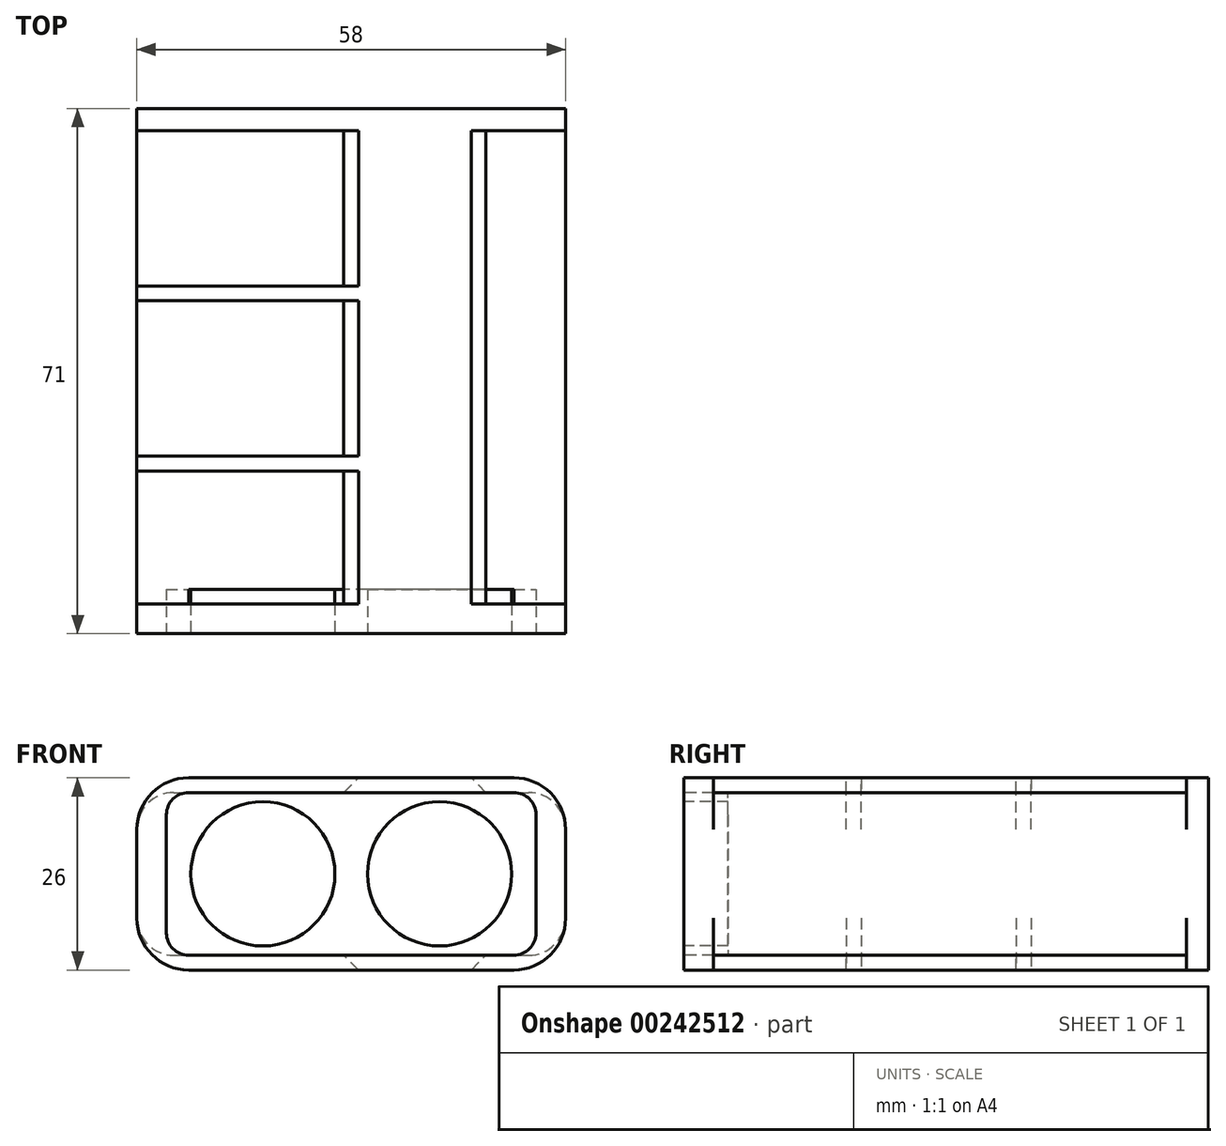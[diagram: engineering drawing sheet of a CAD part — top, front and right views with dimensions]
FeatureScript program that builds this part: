
annotation { "Feature Type Name" : "Feature", "Feature Type Description" : "" }
export const myFeature = defineFeature(function(context is Context, id is Id, definition is map)
    precondition{}
    {
        {
            var Q0;
            Q0=qCreatedBy(makeId("Front.planeOp"),FACE);
            var sketch = newSketch(context, id + "F0", { "sketchPlane" : qUnion([Q0])});
            skLineSegment(sketch, "E0.bottom", {"start": v(25, 11) * mm, "end": v(-25, 11) * mm});
            skLineSegment(sketch, "E0.top", {"start": v(25, -11) * mm, "end": v(-25, -11) * mm});
            skLineSegment(sketch, "E0.left", {"start": v(25, 11) * mm, "end": v(25, -11) * mm});
            skLineSegment(sketch, "E0.right", {"start": v(-25, 11) * mm, "end": v(-25, -11) * mm});
            skPoint(sketch, "E0.middle", {"position": v(0, 0) * mm});
            skCircle(sketch, "E1", {"center": v(-11.95, 0) * mm, "radius": 9.75 * mm});
            skCircle(sketch, "E2.MirrorC", {"center": v(11.95, 0) * mm, "radius": 9.75 * mm});
            skSolve(sketch);
        }
        {
            var Q0;
            Q0 = qSketchRegion(id + "F0", true);
            extrude(context, id + "F1", {"entities" : qUnion([Q0]), "depth" : 71 * mm, "offsetDistance" : 25 * mm, "hasSecondDirection" : true, "secondDirectionOppositeDirection" : false, "secondDirectionDepth" : 65 * mm});
        }
        {
            var Q0;
            Q0=makeQuery(id+"F1.opExtrude","SWEPT_EDGE",EDGE,{"disambiguationData":[OSD([sQuery(id+"F0.wireOp",EDGE,"E0.bottom"),sQuery(id+"F0.wireOp",EDGE,"E0.left")])]});
            var Q1;
            Q1=makeQuery(id+"F1.opExtrude","SWEPT_EDGE",EDGE,{"disambiguationData":[OSD([sQuery(id+"F0.wireOp",EDGE,"E0.top"),sQuery(id+"F0.wireOp",EDGE,"E0.left")])]});
            var Q2;
            Q2=makeQuery(id+"F1.opExtrude","SWEPT_EDGE",EDGE,{"disambiguationData":[OSD([sQuery(id+"F0.wireOp",EDGE,"E0.bottom"),sQuery(id+"F0.wireOp",EDGE,"E0.right")])]});
            var Q3;
            Q3=makeQuery(id+"F1.opExtrude","SWEPT_EDGE",EDGE,{"disambiguationData":[OSD([sQuery(id+"F0.wireOp",EDGE,"E0.top"),sQuery(id+"F0.wireOp",EDGE,"E0.right")])]});
            fillet(context, id + "F2", {"entities" : qUnion([Q0, Q1, Q2, Q3]), "radius" : 3 * mm, "tangentPropagation" : true, "allowEdgeOverflow" : false});
        }
        {
            var Q0;
            Q0=qCreatedBy(makeId("Front.planeOp"),FACE);
            var sketch = newSketch(context, id + "F3", { "sketchPlane" : qUnion([Q0])});
            skLineSegment(sketch, "E3.bottom", {"start": v(-29, 13) * mm, "end": v(29, 13) * mm});
            skLineSegment(sketch, "E3.top", {"start": v(-29, -13) * mm, "end": v(29, -13) * mm});
            skLineSegment(sketch, "E3.left", {"start": v(-29, 13) * mm, "end": v(-29, -13) * mm});
            skLineSegment(sketch, "E3.right", {"start": v(29, 13) * mm, "end": v(29, -13) * mm});
            skPoint(sketch, "E3.middle", {"position": v(0, 0) * mm});
            skSolve(sketch);
        }
        {
            var Q0;
            Q0 = qSketchRegion(id + "F3", true);
            extrude(context, id + "F4", {"entities" : qUnion([Q0]), "depth" : 71 * mm, "offsetDistance" : 25 * mm});
        }
        {
            var Q0;
            Q0=makeQuery(id+"F1.opExtrude","CAP_FACE",FACE,{"disambiguationData":[OSD([sQuery(id+"F0.wireOp",EDGE,"E0.bottom"),sQuery(id+"F0.wireOp",EDGE,"E0.top"),sQuery(id+"F0.wireOp",EDGE,"E0.left"),sQuery(id+"F0.wireOp",EDGE,"E0.right"),sQuery(id+"F0.wireOp",EDGE,"E1"),sQuery(id+"F0.wireOp",EDGE,"E2.MirrorC")])],"isStart":false});
            extrude(context, id + "F5", {"entities" : qUnion([Q0]), "operationType" : NewBodyOperationType.REMOVE, "oppositeDirection" : true, "depth" : 6 * mm, "offsetDistance" : 25 * mm});
        }
        {
            var Q0;
            Q0=makeQuery(id+"F4.opExtrude","SWEPT_EDGE",EDGE,{"disambiguationData":[OSD([sQuery(id+"F3.wireOp",EDGE,"E3.bottom"),sQuery(id+"F3.wireOp",EDGE,"E3.left")])]});
            var Q1;
            Q1=makeQuery(id+"F4.opExtrude","SWEPT_EDGE",EDGE,{"disambiguationData":[OSD([sQuery(id+"F3.wireOp",EDGE,"E3.top"),sQuery(id+"F3.wireOp",EDGE,"E3.left")])]});
            var Q2;
            Q2=makeQuery(id+"F4.opExtrude","SWEPT_EDGE",EDGE,{"disambiguationData":[OSD([sQuery(id+"F3.wireOp",EDGE,"E3.bottom"),sQuery(id+"F3.wireOp",EDGE,"E3.right")])]});
            var Q3;
            Q3=makeQuery(id+"F4.opExtrude","SWEPT_EDGE",EDGE,{"disambiguationData":[OSD([sQuery(id+"F3.wireOp",EDGE,"E3.top"),sQuery(id+"F3.wireOp",EDGE,"E3.right")])]});
            fillet(context, id + "F6", {"entities" : qUnion([Q0, Q1, Q2, Q3]), "radius" : 7 * mm, "tangentPropagation" : true, "allowEdgeOverflow" : false});
        }
        {
            var Q0;
            Q0=qCreatedBy(makeId("Top.planeOp"),FACE);
            var sketch = newSketch(context, id + "F7", { "sketchPlane" : qUnion([Q0])});
            skLineSegment(sketch, "E4", {"start": v(-29, 0) * mm, "end": v(-29, -73) * mm, "construction": true});
            skLineSegment(sketch, "E5.bottom", {"start": v(-54, -3) * mm, "end": v(-4, -3) * mm});
            skLineSegment(sketch, "E5.top", {"start": v(-54, -24) * mm, "end": v(-4, -24) * mm});
            skLineSegment(sketch, "E5.left", {"start": v(-54, -3) * mm, "end": v(-54, -24) * mm});
            skLineSegment(sketch, "E5.right", {"start": v(-4, -3) * mm, "end": v(-4, -24) * mm});
            skPoint(sketch, "E5.middle", {"position": v(-29, -13.5) * mm});
            skLineSegment(sketch, "E6.bottom", {"start": v(-54, -26) * mm, "end": v(-4, -26) * mm});
            skLineSegment(sketch, "E6.top", {"start": v(-54, -47) * mm, "end": v(-4, -47) * mm});
            skLineSegment(sketch, "E6.left", {"start": v(-54, -26) * mm, "end": v(-54, -47) * mm});
            skLineSegment(sketch, "E6.right", {"start": v(-4, -26) * mm, "end": v(-4, -47) * mm});
            skPoint(sketch, "E6.middle", {"position": v(-29, -36.5) * mm});
            skLineSegment(sketch, "E7.bottom", {"start": v(-54, -49) * mm, "end": v(-4, -49) * mm});
            skLineSegment(sketch, "E7.top", {"start": v(-54, -67) * mm, "end": v(-4, -67) * mm});
            skLineSegment(sketch, "E7.left", {"start": v(-54, -49) * mm, "end": v(-54, -67) * mm});
            skLineSegment(sketch, "E7.right", {"start": v(-4, -49) * mm, "end": v(-4, -67) * mm});
            skPoint(sketch, "E7.middle", {"position": v(-29, -58) * mm});
            skLineSegment(sketch, "E8.bottom", {"start": v(21.23, -3) * mm, "end": v(43.23, -3) * mm});
            skLineSegment(sketch, "E8.top", {"start": v(21.23, -67) * mm, "end": v(43.23, -67) * mm});
            skLineSegment(sketch, "E8.left", {"start": v(21.23, -3) * mm, "end": v(21.23, -67) * mm});
            skLineSegment(sketch, "E8.right", {"start": v(43.23, -3) * mm, "end": v(43.23, -67) * mm});
            skPoint(sketch, "E8.middle", {"position": v(32.23, -35) * mm});
            skSolve(sketch);
        }
        {
            var Q0;
            Q0 = qSketchRegion(id + "F7", true);
            extrude(context, id + "F8", {"entities" : qUnion([Q0]), "operationType" : NewBodyOperationType.REMOVE, "oppositeDirection" : true, "depth" : 28.9 * mm, "offsetDistance" : 25 * mm, "hasSecondDirection" : true, "secondDirectionOppositeDirection" : true, "secondDirectionDepth" : 11 * mm});
        }
        {
            var Q0;
            Q0 = qSketchRegion(id + "F7", true);
            extrude(context, id + "F9", {"entities" : qUnion([Q0]), "operationType" : NewBodyOperationType.REMOVE, "depth" : 17.8 * mm, "offsetDistance" : 25 * mm, "hasSecondDirection" : true, "secondDirectionOppositeDirection" : false, "secondDirectionDepth" : 11 * mm});
        }
        {
            var Q0;
            Q0=makeQuery(id+"F9.boolean.opBoolean","INTERSECT",EDGE,{"derivedFrom":[makeQuery(id+"F6.opFillet","BLEND_FACE",FACE,{"disambiguationData":[OSD([sQuery(id+"F3.wireOp",EDGE,"E3.bottom"),sQuery(id+"F3.wireOp",EDGE,"E3.left")])]}),makeQuery(id+"F9.opExtrude","CAP_FACE",FACE,{"disambiguationData":[OSD([sQuery(id+"F7.wireOp",EDGE,"E6.bottom"),sQuery(id+"F7.wireOp",EDGE,"E6.top"),sQuery(id+"F7.wireOp",EDGE,"E6.left"),sQuery(id+"F7.wireOp",EDGE,"E6.right")])],"isStart":true})]});
            var Q1;
            Q1=makeQuery(id+"F9.boolean.opBoolean","INTERSECT",EDGE,{"derivedFrom":[makeQuery(id+"F6.opFillet","BLEND_FACE",FACE,{"disambiguationData":[OSD([sQuery(id+"F3.wireOp",EDGE,"E3.bottom"),sQuery(id+"F3.wireOp",EDGE,"E3.left")])]}),makeQuery(id+"F9.opExtrude","CAP_FACE",FACE,{"disambiguationData":[OSD([sQuery(id+"F7.wireOp",EDGE,"E5.bottom"),sQuery(id+"F7.wireOp",EDGE,"E5.top"),sQuery(id+"F7.wireOp",EDGE,"E5.left"),sQuery(id+"F7.wireOp",EDGE,"E5.right")])],"isStart":true})]});
            var Q2;
            Q2=makeQuery(id+"F9.boolean.opBoolean","INTERSECT",EDGE,{"derivedFrom":[makeQuery(id+"F6.opFillet","BLEND_FACE",FACE,{"disambiguationData":[OSD([sQuery(id+"F3.wireOp",EDGE,"E3.bottom"),sQuery(id+"F3.wireOp",EDGE,"E3.left")])]}),makeQuery(id+"F9.opExtrude","CAP_FACE",FACE,{"disambiguationData":[OSD([sQuery(id+"F7.wireOp",EDGE,"E7.bottom"),sQuery(id+"F7.wireOp",EDGE,"E7.top"),sQuery(id+"F7.wireOp",EDGE,"E7.left"),sQuery(id+"F7.wireOp",EDGE,"E7.right")])],"isStart":true})]});
            var Q3;
            Q3=makeQuery(id+"F9.boolean.opBoolean","INTERSECT",EDGE,{"derivedFrom":[makeQuery(id+"F6.opFillet","BLEND_FACE",FACE,{"disambiguationData":[OSD([sQuery(id+"F3.wireOp",EDGE,"E3.bottom"),sQuery(id+"F3.wireOp",EDGE,"E3.right")])]}),makeQuery(id+"F9.opExtrude","CAP_FACE",FACE,{"disambiguationData":[OSD([sQuery(id+"F7.wireOp",EDGE,"E8.bottom"),sQuery(id+"F7.wireOp",EDGE,"E8.top"),sQuery(id+"F7.wireOp",EDGE,"E8.left"),sQuery(id+"F7.wireOp",EDGE,"E8.right")])],"isStart":true})]});
            var Q4;
            Q4=makeQuery(id+"F8.boolean.opBoolean","INTERSECT",EDGE,{"derivedFrom":[makeQuery(id+"F6.opFillet","BLEND_FACE",FACE,{"disambiguationData":[OSD([sQuery(id+"F3.wireOp",EDGE,"E3.top"),sQuery(id+"F3.wireOp",EDGE,"E3.left")])]}),makeQuery(id+"F8.opExtrude","CAP_FACE",FACE,{"disambiguationData":[OSD([sQuery(id+"F7.wireOp",EDGE,"E5.bottom"),sQuery(id+"F7.wireOp",EDGE,"E5.top"),sQuery(id+"F7.wireOp",EDGE,"E5.left"),sQuery(id+"F7.wireOp",EDGE,"E5.right")])],"isStart":true})]});
            var Q5;
            Q5=makeQuery(id+"F8.boolean.opBoolean","INTERSECT",EDGE,{"derivedFrom":[makeQuery(id+"F6.opFillet","BLEND_FACE",FACE,{"disambiguationData":[OSD([sQuery(id+"F3.wireOp",EDGE,"E3.top"),sQuery(id+"F3.wireOp",EDGE,"E3.left")])]}),makeQuery(id+"F8.opExtrude","CAP_FACE",FACE,{"disambiguationData":[OSD([sQuery(id+"F7.wireOp",EDGE,"E6.bottom"),sQuery(id+"F7.wireOp",EDGE,"E6.top"),sQuery(id+"F7.wireOp",EDGE,"E6.left"),sQuery(id+"F7.wireOp",EDGE,"E6.right")])],"isStart":true})]});
            var Q6;
            Q6=makeQuery(id+"F8.boolean.opBoolean","INTERSECT",EDGE,{"derivedFrom":[makeQuery(id+"F6.opFillet","BLEND_FACE",FACE,{"disambiguationData":[OSD([sQuery(id+"F3.wireOp",EDGE,"E3.top"),sQuery(id+"F3.wireOp",EDGE,"E3.left")])]}),makeQuery(id+"F8.opExtrude","CAP_FACE",FACE,{"disambiguationData":[OSD([sQuery(id+"F7.wireOp",EDGE,"E7.bottom"),sQuery(id+"F7.wireOp",EDGE,"E7.top"),sQuery(id+"F7.wireOp",EDGE,"E7.left"),sQuery(id+"F7.wireOp",EDGE,"E7.right")])],"isStart":true})]});
            var Q7;
            Q7=makeQuery(id+"F8.boolean.opBoolean","INTERSECT",EDGE,{"derivedFrom":[makeQuery(id+"F6.opFillet","BLEND_FACE",FACE,{"disambiguationData":[OSD([sQuery(id+"F3.wireOp",EDGE,"E3.top"),sQuery(id+"F3.wireOp",EDGE,"E3.right")])]}),makeQuery(id+"F8.opExtrude","CAP_FACE",FACE,{"disambiguationData":[OSD([sQuery(id+"F7.wireOp",EDGE,"E8.bottom"),sQuery(id+"F7.wireOp",EDGE,"E8.top"),sQuery(id+"F7.wireOp",EDGE,"E8.left"),sQuery(id+"F7.wireOp",EDGE,"E8.right")])],"isStart":true})]});
            fillet(context, id + "F10", {"entities" : qUnion([Q0, Q1, Q2, Q3, Q4, Q5, Q6, Q7]), "radius" : 5 * mm, "tangentPropagation" : true, "allowEdgeOverflow" : false});
        }
        {
            var Q0;
            Q0=makeQuery(id+"F9.boolean.opBoolean","INTERSECT",EDGE,{"derivedFrom":[makeQuery(id+"F4.opExtrude","SWEPT_FACE",FACE,{"disambiguationData":[OSD([sQuery(id+"F3.wireOp",EDGE,"E3.bottom")])]}),makeQuery(id+"F9.opExtrude","SWEPT_FACE",FACE,{"disambiguationData":[OSD([sQuery(id+"F7.wireOp",EDGE,"E5.right")])]})]});
            var Q1;
            Q1=makeQuery(id+"F9.boolean.opBoolean","INTERSECT",EDGE,{"derivedFrom":[makeQuery(id+"F4.opExtrude","SWEPT_FACE",FACE,{"disambiguationData":[OSD([sQuery(id+"F3.wireOp",EDGE,"E3.bottom")])]}),makeQuery(id+"F9.opExtrude","SWEPT_FACE",FACE,{"disambiguationData":[OSD([sQuery(id+"F7.wireOp",EDGE,"E6.right")])]})]});
            var Q2;
            Q2=makeQuery(id+"F9.boolean.opBoolean","INTERSECT",EDGE,{"derivedFrom":[makeQuery(id+"F4.opExtrude","SWEPT_FACE",FACE,{"disambiguationData":[OSD([sQuery(id+"F3.wireOp",EDGE,"E3.bottom")])]}),makeQuery(id+"F9.opExtrude","SWEPT_FACE",FACE,{"disambiguationData":[OSD([sQuery(id+"F7.wireOp",EDGE,"E7.right")])]})]});
            var Q3;
            Q3=makeQuery(id+"F9.boolean.opBoolean","INTERSECT",EDGE,{"derivedFrom":[makeQuery(id+"F4.opExtrude","SWEPT_FACE",FACE,{"disambiguationData":[OSD([sQuery(id+"F3.wireOp",EDGE,"E3.bottom")])]}),makeQuery(id+"F9.opExtrude","SWEPT_FACE",FACE,{"disambiguationData":[OSD([sQuery(id+"F7.wireOp",EDGE,"E8.left")])]})]});
            var Q4;
            Q4=makeQuery(id+"F8.boolean.opBoolean","INTERSECT",EDGE,{"derivedFrom":[makeQuery(id+"F4.opExtrude","SWEPT_FACE",FACE,{"disambiguationData":[OSD([sQuery(id+"F3.wireOp",EDGE,"E3.top")])]}),makeQuery(id+"F8.opExtrude","SWEPT_FACE",FACE,{"disambiguationData":[OSD([sQuery(id+"F7.wireOp",EDGE,"E5.right")])]})]});
            var Q5;
            Q5=makeQuery(id+"F8.boolean.opBoolean","INTERSECT",EDGE,{"derivedFrom":[makeQuery(id+"F4.opExtrude","SWEPT_FACE",FACE,{"disambiguationData":[OSD([sQuery(id+"F3.wireOp",EDGE,"E3.top")])]}),makeQuery(id+"F8.opExtrude","SWEPT_FACE",FACE,{"disambiguationData":[OSD([sQuery(id+"F7.wireOp",EDGE,"E6.right")])]})]});
            var Q6;
            Q6=makeQuery(id+"F8.boolean.opBoolean","INTERSECT",EDGE,{"derivedFrom":[makeQuery(id+"F4.opExtrude","SWEPT_FACE",FACE,{"disambiguationData":[OSD([sQuery(id+"F3.wireOp",EDGE,"E3.top")])]}),makeQuery(id+"F8.opExtrude","SWEPT_FACE",FACE,{"disambiguationData":[OSD([sQuery(id+"F7.wireOp",EDGE,"E7.right")])]})]});
            var Q7;
            Q7=makeQuery(id+"F8.boolean.opBoolean","INTERSECT",EDGE,{"derivedFrom":[makeQuery(id+"F4.opExtrude","SWEPT_FACE",FACE,{"disambiguationData":[OSD([sQuery(id+"F3.wireOp",EDGE,"E3.top")])]}),makeQuery(id+"F8.opExtrude","SWEPT_FACE",FACE,{"disambiguationData":[OSD([sQuery(id+"F7.wireOp",EDGE,"E8.left")])]})]});
            chamfer(context, id + "F11", {"entities" : qUnion([Q0, Q1, Q2, Q3, Q4, Q5, Q6, Q7]), "width" : 5 * mm, "tangentPropagation" : true});
        }
    });
